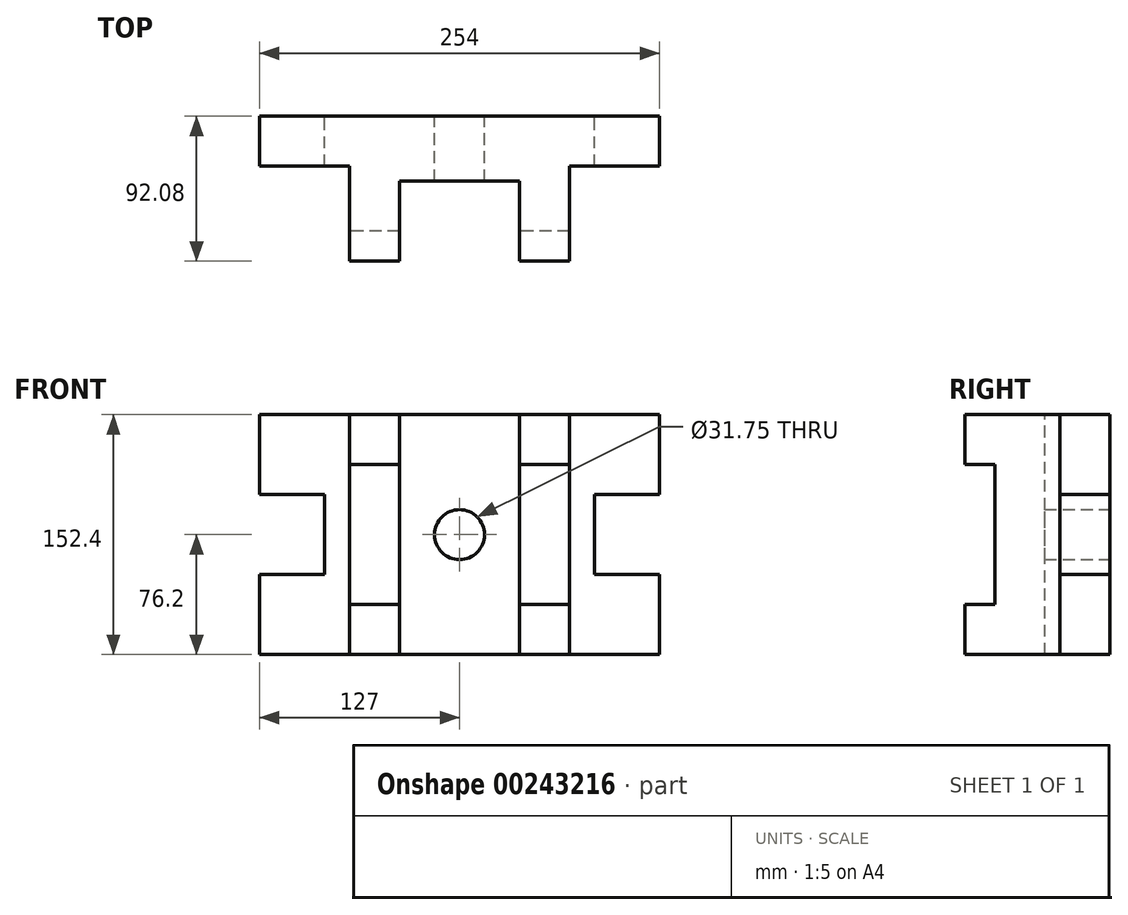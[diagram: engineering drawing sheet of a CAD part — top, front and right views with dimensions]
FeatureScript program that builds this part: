
annotation { "Feature Type Name" : "Feature", "Feature Type Description" : "" }
export const myFeature = defineFeature(function(context is Context, id is Id, definition is map)
    precondition{}
    {
        {
            var Q0;
            Q0=qCreatedBy(makeId("Front.planeOp"),FACE);
            var sketch = newSketch(context, id + "F0", { "sketchPlane" : qUnion([Q0])});
            skLineSegment(sketch, "E0.bottom", {"start": v(-127, 76.2) * mm, "end": v(127, 76.2) * mm});
            skLineSegment(sketch, "E0.top", {"start": v(-127, -76.2) * mm, "end": v(127, -76.2) * mm});
            skLineSegment(sketch, "E0.left", {"start": v(-127, 76.2) * mm, "end": v(-127, 25.4) * mm});
            skLineSegment(sketch, "E0.right", {"start": v(127, 76.2) * mm, "end": v(127, 25.4) * mm});
            skCircle(sketch, "E1", {"center": v(0, 0) * mm, "radius": 15.88 * mm});
            skLineSegment(sketch, "E2.bottom", {"start": v(127, -25.4) * mm, "end": v(85.73, -25.4) * mm});
            skLineSegment(sketch, "E2.top", {"start": v(127, 25.4) * mm, "end": v(85.72, 25.4) * mm});
            skLineSegment(sketch, "E2.right", {"start": v(85.73, -25.4) * mm, "end": v(85.72, 25.4) * mm});
            skLineSegment(sketch, "E3.bottom", {"start": v(-127, 25.4) * mm, "end": v(-85.73, 25.4) * mm});
            skLineSegment(sketch, "E3.top", {"start": v(-127, -25.4) * mm, "end": v(-85.73, -25.4) * mm});
            skLineSegment(sketch, "E3.right", {"start": v(-85.72, 25.4) * mm, "end": v(-85.72, -25.4) * mm});
            skLineSegment(sketch, "E4", {"start": v(-69.85, 76.2) * mm, "end": v(-69.85, -76.2) * mm});
            skLineSegment(sketch, "E5", {"start": v(-38.1, 76.2) * mm, "end": v(-38.1, -76.2) * mm});
            skLineSegment(sketch, "E6", {"start": v(38.1, 76.2) * mm, "end": v(38.1, -76.2) * mm});
            skLineSegment(sketch, "E7", {"start": v(69.85, -76.2) * mm, "end": v(69.85, 76.2) * mm});
            skLineSegment(sketch, "E8.bottom", {"start": v(38.1, -44.45) * mm, "end": v(69.85, -44.45) * mm});
            skLineSegment(sketch, "E8.top", {"start": v(38.1, -76.2) * mm, "end": v(69.85, -76.2) * mm});
            skLineSegment(sketch, "E8.left", {"start": v(38.1, -44.45) * mm, "end": v(38.1, -76.2) * mm});
            skLineSegment(sketch, "E8.right", {"start": v(69.85, -44.45) * mm, "end": v(69.85, -76.2) * mm});
            skLineSegment(sketch, "E9.bottom", {"start": v(-69.85, -44.45) * mm, "end": v(-38.1, -44.45) * mm});
            skLineSegment(sketch, "E9.top", {"start": v(-69.85, -76.2) * mm, "end": v(-38.1, -76.2) * mm});
            skLineSegment(sketch, "E9.left", {"start": v(-69.85, -44.45) * mm, "end": v(-69.85, -76.2) * mm});
            skLineSegment(sketch, "E9.right", {"start": v(-38.1, -44.45) * mm, "end": v(-38.1, -76.2) * mm});
            skLineSegment(sketch, "E10", {"start": v(-69.85, 44.45) * mm, "end": v(-38.1, 44.45) * mm});
            skLineSegment(sketch, "E11", {"start": v(38.1, 44.45) * mm, "end": v(69.85, 44.45) * mm});
            skLineSegment(sketch, "E12.trimOffspring", {"start": v(-127, -25.4) * mm, "end": v(-127, -76.2) * mm});
            skLineSegment(sketch, "E13.trimOffspring", {"start": v(127, -25.4) * mm, "end": v(127, -76.2) * mm});
            skSolve(sketch);
        }
        {
            var Q0;
            {var subQ10=sQuery(id+"F0.wireOp",EDGE,"E3.bottom");Q0=makeQuery(id+"F0.imprint","IMPRINT",FACE,{"disambiguationData":[TD([[makeQuery(id+"F0.imprint","IMPRINT",EDGE,{"derivedFrom":subQ10}),1.0]])]});}
            var Q1;
            Q1=makeQuery(id+"F0.imprint","IMPRINT",FACE,{"disambiguationData":[TD([[makeQuery(id+"F0.imprint","IMPRINT",EDGE,{"derivedFrom":sQuery(id+"F0.wireOp",EDGE,"E1")}),-1.0]])]});
            var Q2;
            {var subQ5=sQuery(id+"F0.wireOp",EDGE,"E10");Q2=makeQuery(id+"F0.imprint","IMPRINT",FACE,{"disambiguationData":[TD([[makeQuery(id+"F0.imprint","IMPRINT",EDGE,{"derivedFrom":subQ5}),1.0]])]});}
            var Q3;
            {var subQ0=sQuery(id+"F0.wireOp",EDGE,"E9.bottom");Q3=makeQuery(id+"F0.imprint","IMPRINT",FACE,{"disambiguationData":[TD([[makeQuery(id+"F0.imprint","IMPRINT",EDGE,{"derivedFrom":subQ0}),1.0]])]});}
            var Q4;
            Q4=makeQuery(id+"F0.imprint","IMPRINT",FACE,{"disambiguationData":[TD([[makeQuery(id+"F0.imprint","IMPRINT",EDGE,{"derivedFrom":sQuery(id+"F0.wireOp",EDGE,"E9.bottom")}),-1.0]])]});
            var Q5;
            Q5=makeQuery(id+"F0.imprint","IMPRINT",FACE,{"disambiguationData":[TD([[makeQuery(id+"F0.imprint","IMPRINT",EDGE,{"derivedFrom":sQuery(id+"F0.wireOp",EDGE,"E8.bottom")}),-1.0]])]});
            var Q6;
            {var subQ0=sQuery(id+"F0.wireOp",EDGE,"E8.bottom");Q6=makeQuery(id+"F0.imprint","IMPRINT",FACE,{"disambiguationData":[TD([[makeQuery(id+"F0.imprint","IMPRINT",EDGE,{"derivedFrom":subQ0}),1.0]])]});}
            var Q7;
            {var subQ5=sQuery(id+"F0.wireOp",EDGE,"E11");Q7=makeQuery(id+"F0.imprint","IMPRINT",FACE,{"disambiguationData":[TD([[makeQuery(id+"F0.imprint","IMPRINT",EDGE,{"derivedFrom":subQ5}),1.0]])]});}
            var Q8;
            {var subQ4=sQuery(id+"F0.wireOp",EDGE,"E2.bottom");Q8=makeQuery(id+"F0.imprint","IMPRINT",FACE,{"disambiguationData":[TD([[makeQuery(id+"F0.imprint","IMPRINT",EDGE,{"derivedFrom":subQ4}),1.0]])]});}
            extrude(context, id + "F1", {"entities" : qUnion([Q0, Q1, Q2, Q3, Q4, Q5, Q6, Q7, Q8]), "depth" : 31.75 * mm});
        }
        {
            var Q0;
            {var subQ5=sQuery(id+"F0.wireOp",EDGE,"E10");Q0=makeQuery(id+"F0.imprint","IMPRINT",FACE,{"disambiguationData":[TD([[makeQuery(id+"F0.imprint","IMPRINT",EDGE,{"derivedFrom":subQ5}),1.0]])]});}
            var Q1;
            {var subQ0=sQuery(id+"F0.wireOp",EDGE,"E9.bottom");Q1=makeQuery(id+"F0.imprint","IMPRINT",FACE,{"disambiguationData":[TD([[makeQuery(id+"F0.imprint","IMPRINT",EDGE,{"derivedFrom":subQ0}),1.0]])]});}
            var Q2;
            Q2=makeQuery(id+"F0.imprint","IMPRINT",FACE,{"disambiguationData":[TD([[makeQuery(id+"F0.imprint","IMPRINT",EDGE,{"derivedFrom":sQuery(id+"F0.wireOp",EDGE,"E1")}),-1.0]])]});
            var Q3;
            Q3=makeQuery(id+"F0.imprint","IMPRINT",FACE,{"disambiguationData":[TD([[makeQuery(id+"F0.imprint","IMPRINT",EDGE,{"derivedFrom":sQuery(id+"F0.wireOp",EDGE,"E9.bottom")}),-1.0]])]});
            var Q4;
            {var subQ5=sQuery(id+"F0.wireOp",EDGE,"E11");Q4=makeQuery(id+"F0.imprint","IMPRINT",FACE,{"disambiguationData":[TD([[makeQuery(id+"F0.imprint","IMPRINT",EDGE,{"derivedFrom":subQ5}),1.0]])]});}
            var Q5;
            {var subQ0=sQuery(id+"F0.wireOp",EDGE,"E8.bottom");Q5=makeQuery(id+"F0.imprint","IMPRINT",FACE,{"disambiguationData":[TD([[makeQuery(id+"F0.imprint","IMPRINT",EDGE,{"derivedFrom":subQ0}),1.0]])]});}
            var Q6;
            Q6=makeQuery(id+"F0.imprint","IMPRINT",FACE,{"disambiguationData":[TD([[makeQuery(id+"F0.imprint","IMPRINT",EDGE,{"derivedFrom":sQuery(id+"F0.wireOp",EDGE,"E8.bottom")}),-1.0]])]});
            extrude(context, id + "F2", {"entities" : qUnion([Q0, Q1, Q2, Q3, Q4, Q5, Q6]), "operationType" : NewBodyOperationType.ADD, "depth" : 41.27 * mm});
        }
        {
            var Q0;
            {var subQ5=sQuery(id+"F0.wireOp",EDGE,"E10");Q0=makeQuery(id+"F0.imprint","IMPRINT",FACE,{"disambiguationData":[TD([[makeQuery(id+"F0.imprint","IMPRINT",EDGE,{"derivedFrom":subQ5}),1.0]])]});}
            var Q1;
            {var subQ0=sQuery(id+"F0.wireOp",EDGE,"E9.bottom");Q1=makeQuery(id+"F0.imprint","IMPRINT",FACE,{"disambiguationData":[TD([[makeQuery(id+"F0.imprint","IMPRINT",EDGE,{"derivedFrom":subQ0}),1.0]])]});}
            var Q2;
            Q2=makeQuery(id+"F0.imprint","IMPRINT",FACE,{"disambiguationData":[TD([[makeQuery(id+"F0.imprint","IMPRINT",EDGE,{"derivedFrom":sQuery(id+"F0.wireOp",EDGE,"E9.bottom")}),-1.0]])]});
            var Q3;
            Q3=makeQuery(id+"F0.imprint","IMPRINT",FACE,{"disambiguationData":[TD([[makeQuery(id+"F0.imprint","IMPRINT",EDGE,{"derivedFrom":sQuery(id+"F0.wireOp",EDGE,"E8.bottom")}),-1.0]])]});
            var Q4;
            {var subQ0=sQuery(id+"F0.wireOp",EDGE,"E8.bottom");Q4=makeQuery(id+"F0.imprint","IMPRINT",FACE,{"disambiguationData":[TD([[makeQuery(id+"F0.imprint","IMPRINT",EDGE,{"derivedFrom":subQ0}),1.0]])]});}
            var Q5;
            {var subQ5=sQuery(id+"F0.wireOp",EDGE,"E11");Q5=makeQuery(id+"F0.imprint","IMPRINT",FACE,{"disambiguationData":[TD([[makeQuery(id+"F0.imprint","IMPRINT",EDGE,{"derivedFrom":subQ5}),1.0]])]});}
            extrude(context, id + "F3", {"entities" : qUnion([Q0, Q1, Q2, Q3, Q4, Q5]), "operationType" : NewBodyOperationType.ADD, "depth" : 73.02 * mm});
        }
        {
            var Q0;
            {var subQ5=sQuery(id+"F0.wireOp",EDGE,"E10");Q0=makeQuery(id+"F0.imprint","IMPRINT",FACE,{"disambiguationData":[TD([[makeQuery(id+"F0.imprint","IMPRINT",EDGE,{"derivedFrom":subQ5}),1.0]])]});}
            var Q1;
            Q1=makeQuery(id+"F0.imprint","IMPRINT",FACE,{"disambiguationData":[TD([[makeQuery(id+"F0.imprint","IMPRINT",EDGE,{"derivedFrom":sQuery(id+"F0.wireOp",EDGE,"E9.bottom")}),-1.0]])]});
            var Q2;
            Q2=makeQuery(id+"F0.imprint","IMPRINT",FACE,{"disambiguationData":[TD([[makeQuery(id+"F0.imprint","IMPRINT",EDGE,{"derivedFrom":sQuery(id+"F0.wireOp",EDGE,"E8.bottom")}),-1.0]])]});
            var Q3;
            {var subQ5=sQuery(id+"F0.wireOp",EDGE,"E11");Q3=makeQuery(id+"F0.imprint","IMPRINT",FACE,{"disambiguationData":[TD([[makeQuery(id+"F0.imprint","IMPRINT",EDGE,{"derivedFrom":subQ5}),1.0]])]});}
            extrude(context, id + "F4", {"entities" : qUnion([Q0, Q1, Q2, Q3]), "operationType" : NewBodyOperationType.ADD, "depth" : 92.07 * mm});
        }
    });
